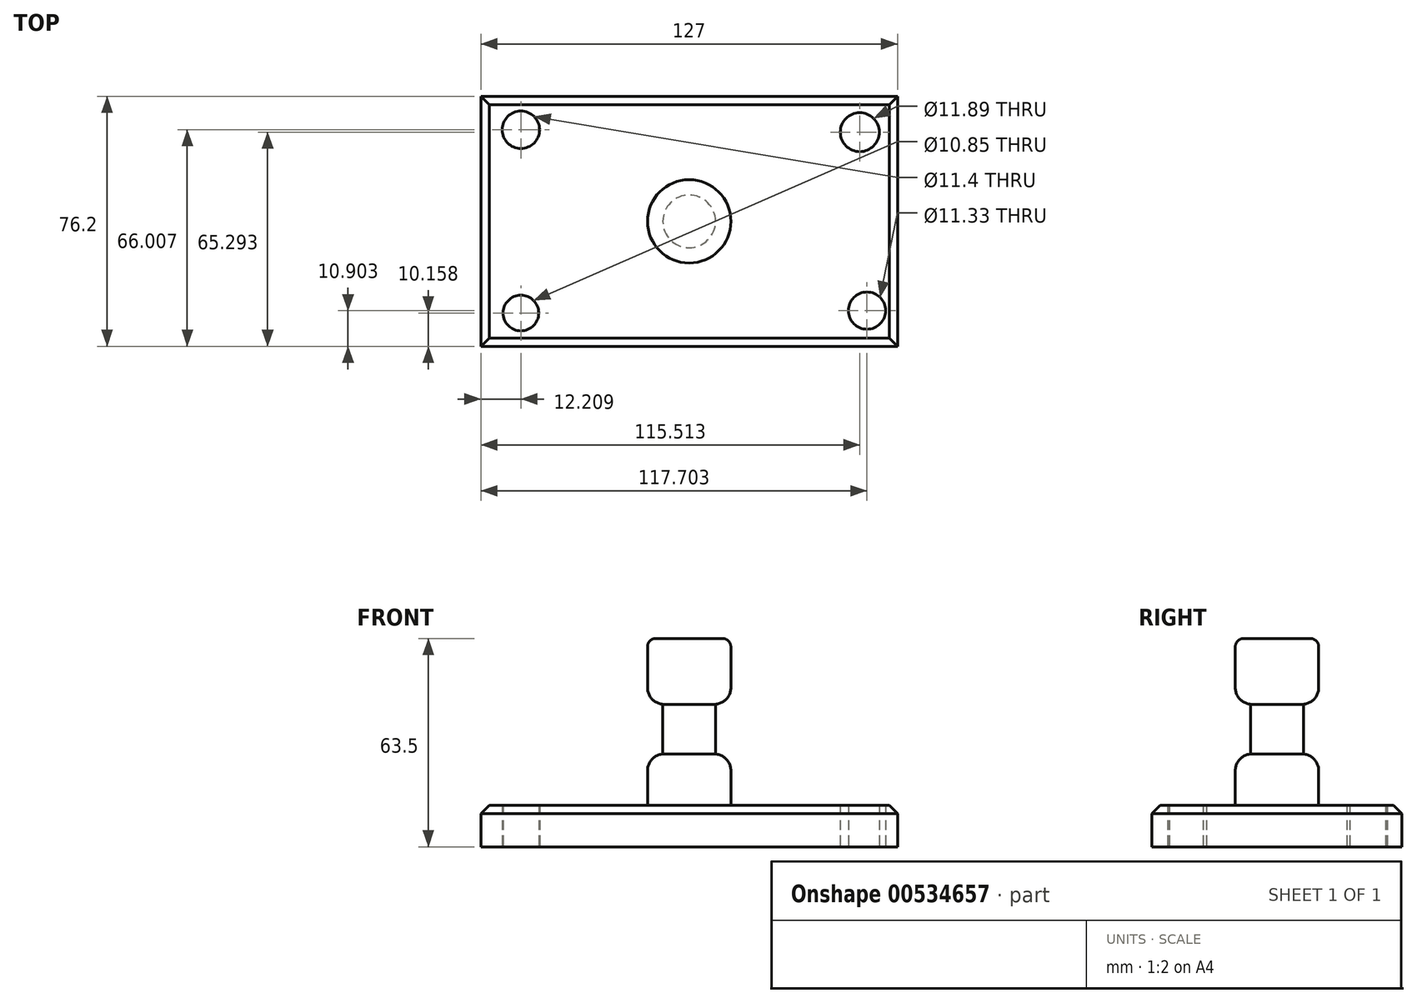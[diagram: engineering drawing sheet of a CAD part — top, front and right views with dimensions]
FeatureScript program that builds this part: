
annotation { "Feature Type Name" : "Feature", "Feature Type Description" : "" }
export const myFeature = defineFeature(function(context is Context, id is Id, definition is map)
    precondition{}
    {
        {
            var Q0;
            Q0=qCreatedBy(makeId("Top.planeOp"),FACE);
            var sketch = newSketch(context, id + "F0", { "sketchPlane" : qUnion([Q0])});
            skLineSegment(sketch, "E0.bottom", {"start": v(63.5, -38.1) * mm, "end": v(-63.5, -38.1) * mm});
            skLineSegment(sketch, "E0.top", {"start": v(63.5, 38.1) * mm, "end": v(-63.5, 38.1) * mm});
            skLineSegment(sketch, "E0.left", {"start": v(63.5, -38.1) * mm, "end": v(63.5, 38.1) * mm});
            skLineSegment(sketch, "E0.right", {"start": v(-63.5, -38.1) * mm, "end": v(-63.5, 38.1) * mm});
            skPoint(sketch, "E0.middle", {"position": v(0, 0) * mm});
            skSolve(sketch);
        }
        {
            var Q0;
            Q0=makeQuery(id+"F0.imprint","IMPRINT",FACE,{"disambiguationData":[TD([[makeQuery(id+"F0.imprint","IMPRINT",EDGE,{"derivedFrom":sQuery(id+"F0.wireOp",EDGE,"E0.bottom")}),-1.0]])]});
            extrude(context, id + "F1", {"entities" : qUnion([Q0]), "depth" : 12.7 * mm, "offsetDistance" : 25.4 * mm});
        }
        {
            var Q0;
            Q0=qCreatedBy(makeId("Top.planeOp"),FACE);
            var sketch = newSketch(context, id + "F2", { "sketchPlane" : qUnion([Q0])});
            skCircle(sketch, "E1", {"center": v(52.01, 27.2) * mm, "radius": 5.94 * mm});
            skCircle(sketch, "E2", {"center": v(-51.3, 27.9) * mm, "radius": 5.7 * mm});
            skCircle(sketch, "E3", {"center": v(54.2, -27.2) * mm, "radius": 5.67 * mm});
            skCircle(sketch, "E4", {"center": v(-51.3, -27.94) * mm, "radius": 5.43 * mm});
            skSolve(sketch);
        }
        {
            var Q0;
            Q0=makeQuery(id+"F2.imprint","IMPRINT",FACE,{"disambiguationData":[TD([[makeQuery(id+"F2.imprint","IMPRINT",EDGE,{"derivedFrom":sQuery(id+"F2.wireOp",EDGE,"E1")}),1.0]])]});
            var Q1;
            Q1=makeQuery(id+"F2.imprint","IMPRINT",FACE,{"disambiguationData":[TD([[makeQuery(id+"F2.imprint","IMPRINT",EDGE,{"derivedFrom":sQuery(id+"F2.wireOp",EDGE,"E3")}),1.0]])]});
            var Q2;
            Q2=makeQuery(id+"F2.imprint","IMPRINT",FACE,{"disambiguationData":[TD([[makeQuery(id+"F2.imprint","IMPRINT",EDGE,{"derivedFrom":sQuery(id+"F2.wireOp",EDGE,"E2")}),1.0]])]});
            var Q3;
            Q3=makeQuery(id+"F2.imprint","IMPRINT",FACE,{"disambiguationData":[TD([[makeQuery(id+"F2.imprint","IMPRINT",EDGE,{"derivedFrom":sQuery(id+"F2.wireOp",EDGE,"E4")}),1.0]])]});
            extrude(context, id + "F3", {"entities" : qUnion([Q0, Q1, Q2, Q3]), "operationType" : NewBodyOperationType.REMOVE, "depth" : 12.7 * mm, "offsetDistance" : 25.4 * mm});
        }
        {
            var Q0;
            Q0=qCreatedBy(makeId("Front.planeOp"),FACE);
            var sketch = newSketch(context, id + "F4", { "sketchPlane" : qUnion([Q0])});
            skLineSegment(sketch, "E5.bottom", {"start": v(0, 12.7) * mm, "end": v(12.7, 12.7) * mm});
            skLineSegment(sketch, "E5.top", {"start": v(0, 63.5) * mm, "end": v(12.7, 63.5) * mm});
            skLineSegment(sketch, "E5.left", {"start": v(0, 12.7) * mm, "end": v(0, 63.5) * mm});
            skLineSegment(sketch, "E5.right", {"start": v(12.7, 12.7) * mm, "end": v(12.7, 63.5) * mm});
            skSolve(sketch);
        }
        {
            var Q0;
            Q0=makeQuery(id+"F4.imprint","IMPRINT",FACE,{"disambiguationData":[TD([[makeQuery(id+"F4.imprint","IMPRINT",EDGE,{"derivedFrom":sQuery(id+"F4.wireOp",EDGE,"E5.bottom")}),1.0]])]});
            var Q1;
            Q1=sQuery(id+"F4.wireOp",EDGE,"E5.left");
            revolve(context, id + "F5", {"operationType" : NewBodyOperationType.ADD, "entities" : qUnion([Q0]), "axis" : qUnion([Q1]), "revolveType" : RevolveType.FULL});
        }
        {
            var Q0;
            Q0=qCreatedBy(makeId("Front.planeOp"),FACE);
            var sketch = newSketch(context, id + "F6", { "sketchPlane" : qUnion([Q0])});
            skLineSegment(sketch, "E6.bottom", {"start": v(8.03, 43.44) * mm, "end": v(17.35, 43.44) * mm});
            skLineSegment(sketch, "E6.top", {"start": v(8.03, 28.3) * mm, "end": v(17.35, 28.3) * mm});
            skLineSegment(sketch, "E6.left", {"start": v(8.03, 43.44) * mm, "end": v(8.03, 28.3) * mm});
            skLineSegment(sketch, "E6.right", {"start": v(17.35, 43.44) * mm, "end": v(17.35, 28.3) * mm});
            skSolve(sketch);
        }
        {
            var Q0;
            Q0=makeQuery(id+"F6.imprint","IMPRINT",FACE,{"disambiguationData":[TD([[makeQuery(id+"F6.imprint","IMPRINT",EDGE,{"derivedFrom":sQuery(id+"F6.wireOp",EDGE,"E6.bottom")}),-1.0]])]});
            var Q1;
            Q1=makeQuery(id+"F5.opRevolve","SWEPT_FACE",FACE,{"disambiguationData":[OSD([sQuery(id+"F4.wireOp",EDGE,"E5.right")])]});
            revolve(context, id + "F7", {"operationType" : NewBodyOperationType.REMOVE, "entities" : qUnion([Q0]), "axis" : qUnion([Q1]), "revolveType" : RevolveType.FULL, "oppositeDirection" : true});
        }
        {
            var Q0;
            Q0=makeQuery(id+"F5.opRevolve","SWEPT_EDGE",EDGE,{"disambiguationData":[OSD([sQuery(id+"F4.wireOp",EDGE,"E5.top"),sQuery(id+"F4.wireOp",EDGE,"E5.right")])]});
            var Q1;
            Q1=makeQuery(id+"F5.opRevolve","SWEPT_EDGE",EDGE,{"disambiguationData":[OSD([sQuery(id+"F4.wireOp",EDGE,"E5.bottom"),sQuery(id+"F4.wireOp",EDGE,"E5.right")])]});
            fillet(context, id + "F8", {"entities" : qUnion([Q0, Q1]), "radius" : 2.54 * mm, "tangentPropagation" : true, "allowEdgeOverflow" : false});
        }
        {
            var Q0;
            Q0=makeQuery(id+"F1.opExtrude","CAP_EDGE",EDGE,{"disambiguationData":[OSD([sQuery(id+"F0.wireOp",EDGE,"E0.bottom")])],"isStart":false});
            var Q1;
            Q1=makeQuery(id+"F1.opExtrude","CAP_EDGE",EDGE,{"disambiguationData":[OSD([sQuery(id+"F0.wireOp",EDGE,"E0.top")])],"isStart":false});
            var Q2;
            Q2=makeQuery(id+"F1.opExtrude","CAP_EDGE",EDGE,{"disambiguationData":[OSD([sQuery(id+"F0.wireOp",EDGE,"E0.left")])],"isStart":false});
            var Q3;
            Q3=makeQuery(id+"F1.opExtrude","CAP_EDGE",EDGE,{"disambiguationData":[OSD([sQuery(id+"F0.wireOp",EDGE,"E0.right")])],"isStart":false});
            chamfer(context, id + "F9", {"entities" : qUnion([Q0, Q1, Q2, Q3]), "width" : 2.54 * mm, "tangentPropagation" : true});
        }
        {
            var Q0;
            Q0=makeQuery(id+"F7.boolean.opBoolean","INTERSECT",EDGE,{"derivedFrom":[makeQuery(id+"F5.opRevolve","SWEPT_FACE",FACE,{"disambiguationData":[OSD([sQuery(id+"F4.wireOp",EDGE,"E5.right")])]}),makeQuery(id+"F7.opRevolve","SWEPT_FACE",FACE,{"disambiguationData":[OSD([sQuery(id+"F6.wireOp",EDGE,"E6.bottom")])]})]});
            var Q1;
            Q1=makeQuery(id+"F7.boolean.opBoolean","INTERSECT",EDGE,{"derivedFrom":[makeQuery(id+"F5.opRevolve","SWEPT_FACE",FACE,{"disambiguationData":[OSD([sQuery(id+"F4.wireOp",EDGE,"E5.right")])]}),makeQuery(id+"F7.opRevolve","SWEPT_FACE",FACE,{"disambiguationData":[OSD([sQuery(id+"F6.wireOp",EDGE,"E6.top")])]})]});
            fillet(context, id + "F10", {"entities" : qUnion([Q0, Q1]), "radius" : 5.08 * mm, "tangentPropagation" : true, "allowEdgeOverflow" : false});
        }
    });
